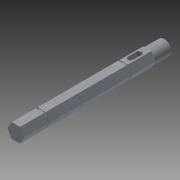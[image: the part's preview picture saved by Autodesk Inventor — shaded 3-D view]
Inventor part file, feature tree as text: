
AUTODESK INVENTOR PART (.ipt)
format: ipt  version: 2014 (Build 180170000, 170)  size: 152,576 bytes
history: native  units: in
note: dims shown in document units (in); Inventor stores cm internally (conversion verified against a paired STEP export)
features: extrude x3, sketch x3, other x1, imported_body x1
ambient origin geometry x8: Origin, YZ Plane, XZ Plane, XY Plane, X Axis, Y Axis, Z Axis, Center Point
bodies: Solid1 (feature_tree)
feature tree (8):
  other  "Shift_Shaft.ipt1"
  extrude  "Extrusion1"  Depth=1.42in TaperAngle=0.0deg
  extrude  "Extrusion2"  [1 undecoded]
  extrude  "Extrusion3"  [1 undecoded]
  imported_body  "Base1"
  sketch  "Sketch1"  dims[d0=1.47in d1=0.0in d2=1.42in d3=0.0in]
  sketch  "Sketch2"  dims[d4=0.57in d5=0.0in]
  sketch  "Sketch3"
note: 2 required parameter values undecoded (feature->parameter linkage not recoverable at this tier; creation-order binding heuristic only, values carry confidence <= 0.55)
